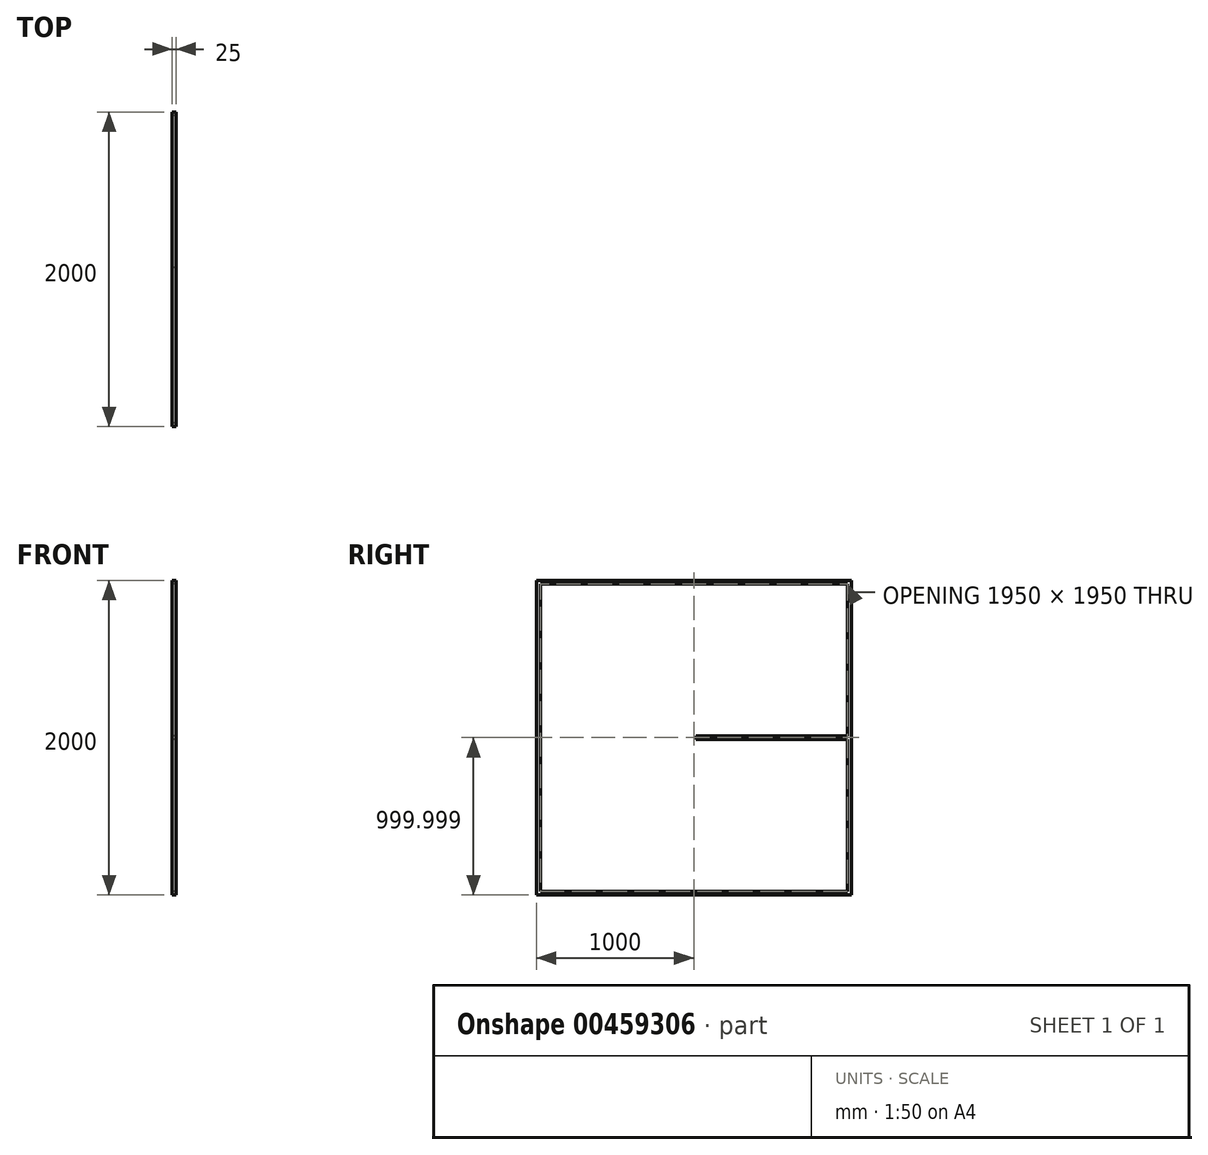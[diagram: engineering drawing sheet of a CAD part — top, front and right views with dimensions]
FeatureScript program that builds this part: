
annotation { "Feature Type Name" : "Feature", "Feature Type Description" : "" }
export const myFeature = defineFeature(function(context is Context, id is Id, definition is map)
    precondition{}
    {
        {
            var Q0;
            Q0=qCreatedBy(makeId("Right.planeOp"),FACE);
            var sketch = newSketch(context, id + "F0", { "sketchPlane" : qUnion([Q0])});
            skLineSegment(sketch, "E0.bottom", {"start": v(-1956.06, 1981.5) * mm, "end": v(43.94, 1981.5) * mm});
            skLineSegment(sketch, "E0.top", {"start": v(-1956.06, -18.5) * mm, "end": v(43.94, -18.5) * mm});
            skLineSegment(sketch, "E0.left", {"start": v(-1956.06, 1981.5) * mm, "end": v(-1956.06, -18.5) * mm});
            skLineSegment(sketch, "E0.right", {"start": v(43.94, 1981.5) * mm, "end": v(43.94, -18.5) * mm});
            skLineSegment(sketch, "E1.bottom", {"start": v(18.94, 6.5) * mm, "end": v(-1931.06, 6.5) * mm});
            skLineSegment(sketch, "E1.top", {"start": v(18.94, 1956.5) * mm, "end": v(-1931.06, 1956.5) * mm});
            skLineSegment(sketch, "E1.left", {"start": v(18.94, 6.5) * mm, "end": v(18.94, 1956.5) * mm});
            skLineSegment(sketch, "E1.right", {"start": v(-1931.06, 6.5) * mm, "end": v(-1931.06, 1956.5) * mm});
            skLineSegment(sketch, "E2", {"start": v(18.94, 6.5) * mm, "end": v(43.94, -18.5) * mm});
            skLineSegment(sketch, "E3", {"start": v(18.94, 1956.5) * mm, "end": v(43.94, 1981.5) * mm});
            skPoint(sketch, "E4.end.orphan", {"position": v(-1931.06, 1932.02) * mm});
            skPoint(sketch, "E5.start.orphan", {"position": v(-1931.06, 1981.5) * mm});
            skLineSegment(sketch, "E6", {"start": v(-1931.06, 1956.5) * mm, "end": v(-1956.06, 1981.5) * mm});
            skLineSegment(sketch, "E7", {"start": v(-1931.06, 6.5) * mm, "end": v(-1956.06, -18.5) * mm});
            skLineSegment(sketch, "E8.bottom", {"start": v(-968.56, 6.5) * mm, "end": v(-943.56, 6.5) * mm});
            skLineSegment(sketch, "E8.top", {"start": v(-968.56, 1956.5) * mm, "end": v(-943.56, 1956.5) * mm});
            skLineSegment(sketch, "E8.left", {"start": v(-968.56, 6.5) * mm, "end": v(-968.56, 1956.5) * mm});
            skLineSegment(sketch, "E8.right", {"start": v(-943.56, 6.5) * mm, "end": v(-943.56, 1956.5) * mm});
            skPoint(sketch, "E8.middle", {"position": v(-956.06, 981.5) * mm});
            skPoint(sketch, "E9.orphan", {"position": v(-956.06, 1981.5) * mm});
            skPoint(sketch, "E10.end.orphan", {"position": v(-956.06, -18.5) * mm});
            skLineSegment(sketch, "E11.bottom", {"start": v(18.94, 994) * mm, "end": v(-943.56, 994) * mm});
            skLineSegment(sketch, "E11.top", {"start": v(18.94, 969) * mm, "end": v(-943.56, 969) * mm});
            skLineSegment(sketch, "E11.left", {"start": v(18.94, 994) * mm, "end": v(18.94, 969) * mm});
            skLineSegment(sketch, "E11.right", {"start": v(-1931.06, 994) * mm, "end": v(-1931.06, 969) * mm});
            skLineSegment(sketch, "E12.trimOffspring", {"start": v(-968.56, 994) * mm, "end": v(-1931.06, 994) * mm});
            skLineSegment(sketch, "E13.trimOffspring", {"start": v(-968.56, 969) * mm, "end": v(-1931.06, 969) * mm});
            skPoint(sketch, "E14.trimOffspring.end.orphan", {"position": v(43.94, 981.5) * mm});
            skPoint(sketch, "E15.start.orphan", {"position": v(-1956.06, 981.5) * mm});
            skSolve(sketch);
        }
        {
            var Q0;
            Q0 = qSketchRegion(id + "F0", true);
            var Q1;
            Q1=makeQuery(id+"F0.imprint","IMPRINT",FACE,{"disambiguationData":[TD([[makeQuery(id+"F0.imprint","IMPRINT",EDGE,{"derivedFrom":sQuery(id+"F0.wireOp",EDGE,"E11.right")}),1.0]])]});
            var Q2;
            {var subQ3=sQuery(id+"F0.wireOp",EDGE,"E8.bottom");Q2=makeQuery(id+"F0.imprint","IMPRINT",FACE,{"disambiguationData":[TD([[makeQuery(id+"F0.imprint","IMPRINT",EDGE,{"derivedFrom":subQ3}),1.0]])]});}
            var Q3;
            {var subQ0=sQuery(id+"F0.wireOp",EDGE,"E11.bottom");Q3=makeQuery(id+"F0.imprint","IMPRINT",FACE,{"disambiguationData":[TD([[makeQuery(id+"F0.imprint","IMPRINT",EDGE,{"derivedFrom":subQ0}),1.0]])]});}
            extrude(context, id + "F1", {"entities" : qUnion([Q0, Q1, Q2, Q3]), "depth" : 25 * mm});
        }
    });
